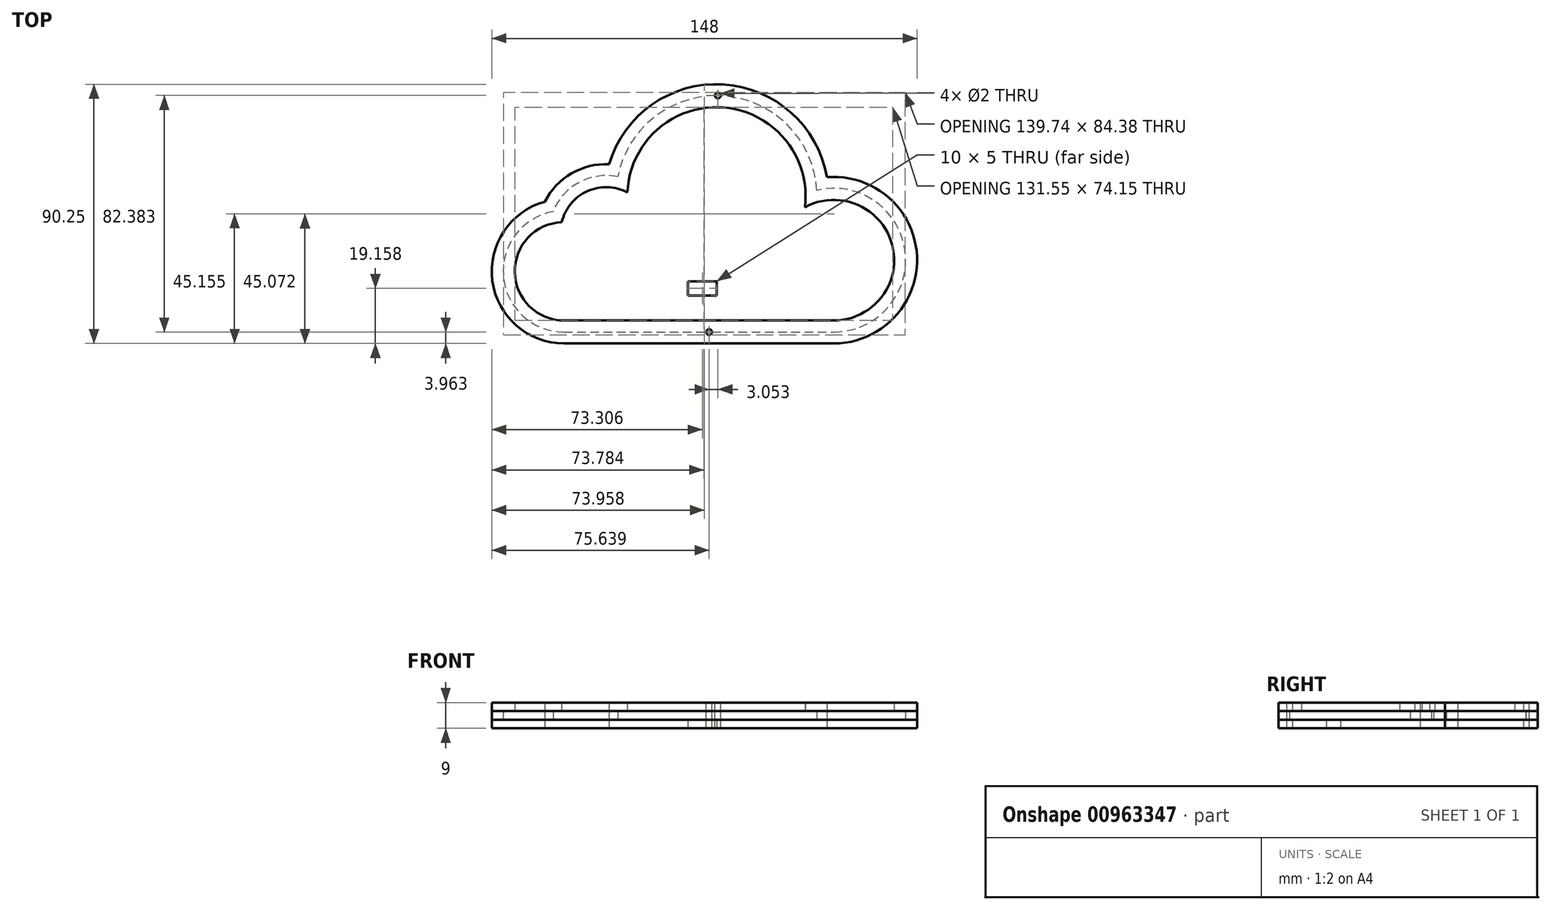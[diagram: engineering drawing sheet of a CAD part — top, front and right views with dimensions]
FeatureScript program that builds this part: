
annotation { "Feature Type Name" : "Feature", "Feature Type Description" : "" }
export const myFeature = defineFeature(function(context is Context, id is Id, definition is map)
    precondition{}
    {
        {
            var Q0;
            Q0=qCreatedBy(makeId("Top.planeOp"),FACE);
            var sketch = newSketch(context, id + "F0", { "sketchPlane" : qUnion([Q0])});
            skArc(sketch, "E0", {"start": v(-76.35, 10.52) * mm, "mid": v(-93.61, -12.15) * mm, "end": v(-72.58, -31.37) * mm});
            skArc(sketch, "E1", {"start": v(15.44, 17.93) * mm, "mid": v(-17.14, 50.8) * mm, "end": v(-53.86, 22.64) * mm});
            skArc(sketch, "E2", {"start": v(21.3, -31.37) * mm, "mid": v(46.13, -3.42) * mm, "end": v(15.44, 17.93) * mm});
            skLineSegment(sketch, "E3", {"start": v(-72.58, -31.37) * mm, "end": v(21.3, -31.37) * mm});
            skArc(sketch, "E4.trimOffspring", {"start": v(-53.86, 22.64) * mm, "mid": v(-67.32, 20.7) * mm, "end": v(-76.35, 10.52) * mm});
            skLineSegment(sketch, "E5", {"start": v(-93.7, 24.07) * mm, "end": v(-93.7, -50.96) * mm, "construction": true});
            skLineSegment(sketch, "E6", {"start": v(46.3, 32.04) * mm, "end": v(46.3, -61.64) * mm, "construction": true});
            skArc(sketch, "E7.0", {"start": v(-56.9, 27.04) * mm, "mid": v(-69.96, 23.8) * mm, "end": v(-79.18, 13.98) * mm});
            skArc(sketch, "E7.1", {"start": v(18.92, 22.53) * mm, "mid": v(-17.2, 54.82) * mm, "end": v(-56.9, 27.04) * mm});
            skArc(sketch, "E7.2", {"start": v(-79.18, 13.98) * mm, "mid": v(-97.47, -13.59) * mm, "end": v(-72.58, -35.37) * mm});
            skLineSegment(sketch, "E7.3", {"start": v(-72.58, -35.37) * mm, "end": v(21.3, -35.37) * mm});
            skArc(sketch, "E7.4", {"start": v(21.3, -35.37) * mm, "mid": v(50.28, -5.18) * mm, "end": v(18.92, 22.53) * mm});
            skArc(sketch, "E8.0", {"start": v(21.3, -27.37) * mm, "mid": v(41.65, -1.2) * mm, "end": v(11.26, 12.07) * mm});
            skLineSegment(sketch, "E8.1", {"start": v(-72.58, -27.37) * mm, "end": v(21.3, -27.37) * mm});
            skArc(sketch, "E8.2", {"start": v(11.26, 12.07) * mm, "mid": v(-16.94, 46.78) * mm, "end": v(-50.5, 17.2) * mm});
            skArc(sketch, "E8.3", {"start": v(-50.5, 17.2) * mm, "mid": v(-64.46, 17.65) * mm, "end": v(-73.32, 6.85) * mm});
            skArc(sketch, "E8.4", {"start": v(-73.32, 6.85) * mm, "mid": v(-89.7, -10.63) * mm, "end": v(-72.58, -27.37) * mm});
            skSolve(sketch);
        }
        {
            var Q0;
            Q0=qCreatedBy(makeId("Top.planeOp"),FACE);
            var sketch = newSketch(context, id + "F1", { "sketchPlane" : qUnion([Q0])});
            skArc(sketch, "E9.0", {"start": v(-56.9, 27.04) * mm, "mid": v(-69.96, 23.8) * mm, "end": v(-79.18, 13.98) * mm});
            skArc(sketch, "E9.1", {"start": v(18.92, 22.53) * mm, "mid": v(-17.2, 54.82) * mm, "end": v(-56.9, 27.04) * mm});
            skArc(sketch, "E9.2", {"start": v(21.3, -35.37) * mm, "mid": v(50.28, -5.18) * mm, "end": v(18.92, 22.53) * mm});
            skLineSegment(sketch, "E9.3", {"start": v(-72.58, -35.37) * mm, "end": v(21.3, -35.37) * mm});
            skArc(sketch, "E9.4", {"start": v(-79.18, 13.98) * mm, "mid": v(-97.47, -13.59) * mm, "end": v(-72.58, -35.37) * mm});
            skLineSegment(sketch, "E10.bottom", {"start": v(-19.4, -18.71) * mm, "end": v(-29.4, -18.71) * mm});
            skLineSegment(sketch, "E10.top", {"start": v(-19.4, -13.71) * mm, "end": v(-29.4, -13.71) * mm});
            skLineSegment(sketch, "E10.left", {"start": v(-19.4, -18.71) * mm, "end": v(-19.4, -13.71) * mm});
            skLineSegment(sketch, "E10.right", {"start": v(-29.4, -18.71) * mm, "end": v(-29.4, -13.71) * mm});
            skPoint(sketch, "E10.middle", {"position": v(-24.4, -16.21) * mm});
            skSolve(sketch);
        }
        {
            var Q0;
            Q0 = qSketchRegion(id + "F1", true);
            extrude(context, id + "F2", {"entities" : qUnion([Q0]), "depth" : 3 * mm, "offsetDistance" : 25 * mm});
        }
        {
            var Q0;
            Q0=makeQuery(id+"F2.opExtrude","CAP_FACE",FACE,{"disambiguationData":[OSD([sQuery(id+"F1.wireOp",EDGE,"E9.0"),sQuery(id+"F1.wireOp",EDGE,"E9.1"),sQuery(id+"F1.wireOp",EDGE,"E9.2"),sQuery(id+"F1.wireOp",EDGE,"E9.3"),sQuery(id+"F1.wireOp",EDGE,"E9.4")])],"isStart":false});
            var sketch = newSketch(context, id + "F3", { "sketchPlane" : qUnion([Q0])});
            skArc(sketch, "E11.0", {"start": v(-53.86, 22.64) * mm, "mid": v(-67.32, 20.7) * mm, "end": v(-76.35, 10.52) * mm});
            skArc(sketch, "E11.1", {"start": v(15.44, 17.93) * mm, "mid": v(-17.14, 50.8) * mm, "end": v(-53.86, 22.64) * mm});
            skArc(sketch, "E11.2", {"start": v(18.92, 22.53) * mm, "mid": v(-17.2, 54.82) * mm, "end": v(-56.9, 27.04) * mm});
            skArc(sketch, "E11.3", {"start": v(-56.9, 27.04) * mm, "mid": v(-69.96, 23.8) * mm, "end": v(-79.18, 13.98) * mm});
            skArc(sketch, "E11.4", {"start": v(-79.18, 13.98) * mm, "mid": v(-97.47, -13.59) * mm, "end": v(-72.58, -35.37) * mm});
            skArc(sketch, "E11.5", {"start": v(-76.35, 10.52) * mm, "mid": v(-93.61, -12.15) * mm, "end": v(-72.58, -31.37) * mm});
            skLineSegment(sketch, "E11.6", {"start": v(-72.58, -31.37) * mm, "end": v(21.3, -31.37) * mm});
            skLineSegment(sketch, "E11.7", {"start": v(-72.58, -35.37) * mm, "end": v(21.3, -35.37) * mm});
            skArc(sketch, "E11.8", {"start": v(21.3, -35.37) * mm, "mid": v(50.28, -5.18) * mm, "end": v(18.92, 22.53) * mm});
            skArc(sketch, "E11.9", {"start": v(21.3, -31.37) * mm, "mid": v(46.13, -3.42) * mm, "end": v(15.44, 17.93) * mm});
            skLineSegment(sketch, "E12", {"start": v(-22.08, -31.37) * mm, "end": v(-22.08, -35.37) * mm, "construction": true});
            skPoint(sketch, "E12.endSnap0", {"position": v(-25.64, -35.37) * mm});
            skPoint(sketch, "E13", {"position": v(-22.08, -33.37) * mm});
            skSolve(sketch);
        }
        {
            var Q0;
            Q0 = qSketchRegion(id + "F3", true);
            extrude(context, id + "F4", {"entities" : qUnion([Q0]), "depth" : 3 * mm, "offsetDistance" : 25 * mm});
        }
        {
            var Q0;
            Q0=makeQuery(id+"F4.opExtrude","CAP_FACE",FACE,{"disambiguationData":[OSD([sQuery(id+"F3.wireOp",EDGE,"E11.0"),sQuery(id+"F3.wireOp",EDGE,"E11.1"),sQuery(id+"F3.wireOp",EDGE,"E11.2"),sQuery(id+"F3.wireOp",EDGE,"E11.3"),sQuery(id+"F3.wireOp",EDGE,"E11.4"),sQuery(id+"F3.wireOp",EDGE,"E11.5"),sQuery(id+"F3.wireOp",EDGE,"E11.6"),sQuery(id+"F3.wireOp",EDGE,"E11.7"),sQuery(id+"F3.wireOp",EDGE,"E11.8"),sQuery(id+"F3.wireOp",EDGE,"E11.9")])],"isStart":false});
            var sketch = newSketch(context, id + "F5", { "sketchPlane" : qUnion([Q0])});
            skArc(sketch, "E14.0", {"start": v(-50.5, 17.2) * mm, "mid": v(-64.46, 17.65) * mm, "end": v(-73.32, 6.85) * mm});
            skArc(sketch, "E14.1", {"start": v(11.26, 12.07) * mm, "mid": v(-16.94, 46.78) * mm, "end": v(-50.5, 17.2) * mm});
            skArc(sketch, "E14.2", {"start": v(21.3, -27.37) * mm, "mid": v(41.65, -1.2) * mm, "end": v(11.26, 12.07) * mm});
            skLineSegment(sketch, "E14.3", {"start": v(-72.58, -27.37) * mm, "end": v(21.3, -27.37) * mm});
            skArc(sketch, "E14.4", {"start": v(-73.32, 6.85) * mm, "mid": v(-89.7, -10.63) * mm, "end": v(-72.58, -27.37) * mm});
            skArc(sketch, "E14.5", {"start": v(-56.9, 27.04) * mm, "mid": v(-69.96, 23.8) * mm, "end": v(-79.18, 13.98) * mm});
            skArc(sketch, "E14.6", {"start": v(18.92, 22.53) * mm, "mid": v(-17.2, 54.82) * mm, "end": v(-56.9, 27.04) * mm});
            skArc(sketch, "E14.7", {"start": v(21.3, -35.37) * mm, "mid": v(50.28, -5.18) * mm, "end": v(18.92, 22.53) * mm});
            skLineSegment(sketch, "E14.8", {"start": v(-72.58, -35.37) * mm, "end": v(21.3, -35.37) * mm});
            skArc(sketch, "E14.9", {"start": v(-79.18, 13.98) * mm, "mid": v(-97.47, -13.59) * mm, "end": v(-72.58, -35.37) * mm});
            skSolve(sketch);
        }
        {
            var Q0;
            Q0 = qSketchRegion(id + "F5", true);
            extrude(context, id + "F6", {"entities" : qUnion([Q0]), "depth" : 3 * mm, "offsetDistance" : 25 * mm});
        }
        {
            var Q0;
            Q0=makeQuery(id+"F6.opExtrude","CAP_FACE",FACE,{"disambiguationData":[OSD([sQuery(id+"F5.wireOp",EDGE,"E14.0"),sQuery(id+"F5.wireOp",EDGE,"E14.1"),sQuery(id+"F5.wireOp",EDGE,"E14.2"),sQuery(id+"F5.wireOp",EDGE,"E14.3"),sQuery(id+"F5.wireOp",EDGE,"E14.4"),sQuery(id+"F5.wireOp",EDGE,"E14.5"),sQuery(id+"F5.wireOp",EDGE,"E14.6"),sQuery(id+"F5.wireOp",EDGE,"E14.7"),sQuery(id+"F5.wireOp",EDGE,"E14.8"),sQuery(id+"F5.wireOp",EDGE,"E14.9")])],"isStart":false});
            var sketch = newSketch(context, id + "F7", { "sketchPlane" : qUnion([Q0])});
            skPoint(sketch, "E15.0", {"position": v(-22.08, -33.37) * mm});
            skCircle(sketch, "E16", {"center": v(-22.06, -31.4) * mm, "radius": 1 * mm});
            skPoint(sketch, "E17", {"position": v(-19, 50.98) * mm});
            skCircle(sketch, "E18", {"center": v(-19, 50.98) * mm, "radius": 1 * mm});
            skSolve(sketch);
        }
        {
            var Q0;
            Q0 = qSketchRegion(id + "F7", true);
            extrude(context, id + "F8", {"entities" : qUnion([Q0]), "operationType" : NewBodyOperationType.REMOVE, "endBound" : BoundingType.THROUGH_ALL, "oppositeDirection" : true, "depth" : 25 * mm, "offsetDistance" : 25 * mm});
        }
    });
